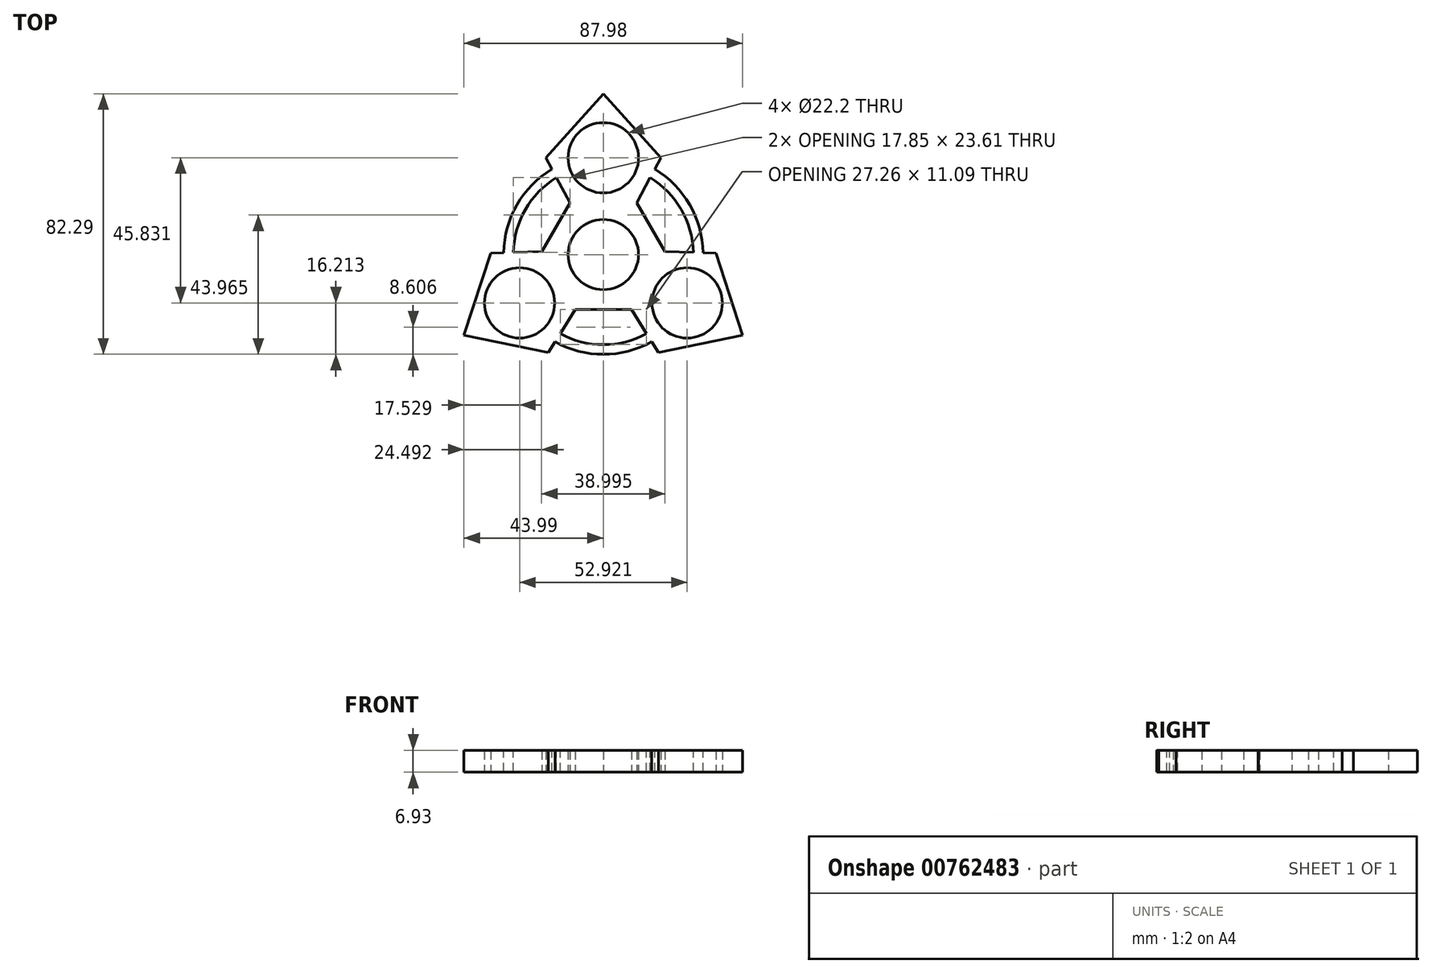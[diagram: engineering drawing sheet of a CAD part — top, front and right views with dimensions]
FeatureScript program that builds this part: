
annotation { "Feature Type Name" : "Feature", "Feature Type Description" : "" }
export const myFeature = defineFeature(function(context is Context, id is Id, definition is map)
    precondition{}
    {
        {
            var Q0;
            Q0=qCreatedBy(makeId("Top.planeOp"),FACE);
            var sketch = newSketch(context, id + "F0", { "sketchPlane" : qUnion([Q0])});
            skCircle(sketch, "E0", {"center": v(0, 0) * mm, "radius": 11.1 * mm});
            skLineSegment(sketch, "E1", {"start": v(0, 50.8) * mm, "end": v(18.14, 30.55) * mm});
            skLineSegment(sketch, "E2", {"start": v(18.14, 30.55) * mm, "end": v(10.57, 16.36) * mm});
            skLineSegment(sketch, "E3.MirrorCS", {"start": v(0, 50.8) * mm, "end": v(-18.14, 30.55) * mm});
            skLineSegment(sketch, "E4.MirrorCS", {"start": v(-18.14, 30.55) * mm, "end": v(-10.57, 16.36) * mm});
            skPoint(sketch, "E5.center.orphan", {"position": v(0, 30.55) * mm});
            skCircle(sketch, "E6", {"center": v(0, 30.55) * mm, "radius": 11.1 * mm});
            skLineSegment(sketch, "E7.1.0", {"start": v(-44, -25.4) * mm, "end": v(-35.53, 0.43) * mm});
            skLineSegment(sketch, "E7.1.1", {"start": v(-44, -25.4) * mm, "end": v(-17.4, -30.98) * mm});
            skCircle(sketch, "E7.1.2", {"center": v(-26.46, -15.28) * mm, "radius": 11.1 * mm});
            skLineSegment(sketch, "E7.1.3", {"start": v(-35.53, 0.43) * mm, "end": v(-19.46, 0.98) * mm});
            skLineSegment(sketch, "E7.1.4", {"start": v(-17.4, -30.98) * mm, "end": v(-8.88, -17.34) * mm});
            skLineSegment(sketch, "E7.2.0", {"start": v(44, -25.4) * mm, "end": v(17.4, -30.98) * mm});
            skLineSegment(sketch, "E7.2.1", {"start": v(44, -25.4) * mm, "end": v(35.53, 0.43) * mm});
            skCircle(sketch, "E7.2.2", {"center": v(26.46, -15.28) * mm, "radius": 11.1 * mm});
            skLineSegment(sketch, "E7.2.3", {"start": v(17.4, -30.98) * mm, "end": v(8.88, -17.34) * mm});
            skLineSegment(sketch, "E7.2.4", {"start": v(35.53, 0.43) * mm, "end": v(19.46, 0.98) * mm});
            skLineSegment(sketch, "E8", {"start": v(10.57, 16.36) * mm, "end": v(19.46, 0.98) * mm});
            skLineSegment(sketch, "E9", {"start": v(8.88, -17.34) * mm, "end": v(-8.88, -17.34) * mm});
            skLineSegment(sketch, "E10", {"start": v(-19.46, 0.98) * mm, "end": v(-10.57, 16.36) * mm});
            skSolve(sketch);
        }
        {
            var Q0;
            Q0=makeQuery(id+"F0.imprint","IMPRINT",FACE,{"disambiguationData":[TD([[makeQuery(id+"F0.imprint","IMPRINT",EDGE,{"derivedFrom":sQuery(id+"F0.wireOp",EDGE,"E0")}),-1.0]])]});
            extrude(context, id + "F1", {"entities" : qUnion([Q0]), "depth" : 6.93 * mm, "offsetDistance" : 25.4 * mm});
        }
        {
            var Q0;
            Q0=makeQuery(id+"F1.opExtrude","CAP_FACE",FACE,{"disambiguationData":[OSD([sQuery(id+"F0.wireOp",EDGE,"E0"),sQuery(id+"F0.wireOp",EDGE,"E1"),sQuery(id+"F0.wireOp",EDGE,"E2"),sQuery(id+"F0.wireOp",EDGE,"E3.MirrorCS"),sQuery(id+"F0.wireOp",EDGE,"E4.MirrorCS"),sQuery(id+"F0.wireOp",EDGE,"E6"),sQuery(id+"F0.wireOp",EDGE,"E7.1.0"),sQuery(id+"F0.wireOp",EDGE,"E7.1.1"),sQuery(id+"F0.wireOp",EDGE,"E7.1.2"),sQuery(id+"F0.wireOp",EDGE,"E7.1.3"),sQuery(id+"F0.wireOp",EDGE,"E7.1.4"),sQuery(id+"F0.wireOp",EDGE,"E7.2.0"),sQuery(id+"F0.wireOp",EDGE,"E7.2.1"),sQuery(id+"F0.wireOp",EDGE,"E7.2.2"),sQuery(id+"F0.wireOp",EDGE,"E7.2.3"),sQuery(id+"F0.wireOp",EDGE,"E7.2.4"),sQuery(id+"F0.wireOp",EDGE,"E8"),sQuery(id+"F0.wireOp",EDGE,"E9"),sQuery(id+"F0.wireOp",EDGE,"E10")])],"isStart":false});
            var sketch = newSketch(context, id + "F2", { "sketchPlane" : qUnion([Q0])});
            skCircle(sketch, "E11", {"center": v(0, 0) * mm, "radius": 28.43 * mm});
            skCircle(sketch, "E12", {"center": v(0, 0) * mm, "radius": 31.5 * mm});
            skSolve(sketch);
        }
        {
            var Q0;
            {var subQ0=sQuery(id+"F2.wireOp",EDGE,"E11");var subQ1=makeQuery(id+"F1.opExtrude","CAP_EDGE",EDGE,{"disambiguationData":[OSD([sQuery(id+"F0.wireOp",EDGE,"E7.1.4")])],"isStart":false});var subQ2=makeQuery(id+"F2.imprint","INTERSECT",VERTEX,{"derivedFrom":[subQ1,subQ0]});Q0=makeQuery(id+"F2.imprint","IMPRINT",FACE,{"disambiguationData":[TD([[makeQuery(id+"F2.imprint","IMPRINT",EDGE,{"disambiguationData":[TD([[subQ2,-1.0]])],"derivedFrom":subQ0}),-1.0]])]});}
            var Q1;
            {var subQ0=sQuery(id+"F2.wireOp",EDGE,"E11");var subQ1=makeQuery(id+"F1.opExtrude","CAP_EDGE",EDGE,{"disambiguationData":[OSD([sQuery(id+"F0.wireOp",EDGE,"E2")])],"isStart":false});var subQ2=makeQuery(id+"F2.imprint","INTERSECT",VERTEX,{"derivedFrom":[subQ1,subQ0]});Q1=makeQuery(id+"F2.imprint","IMPRINT",FACE,{"disambiguationData":[TD([[makeQuery(id+"F2.imprint","IMPRINT",EDGE,{"disambiguationData":[TD([[subQ2,1.0]])],"derivedFrom":subQ0}),-1.0]])]});}
            var Q2;
            {var subQ0=sQuery(id+"F2.wireOp",EDGE,"E11");var subQ1=makeQuery(id+"F1.opExtrude","CAP_EDGE",EDGE,{"disambiguationData":[OSD([sQuery(id+"F0.wireOp",EDGE,"E4.MirrorCS")])],"isStart":false});var subQ2=makeQuery(id+"F2.imprint","INTERSECT",VERTEX,{"derivedFrom":[subQ1,subQ0]});Q2=makeQuery(id+"F2.imprint","IMPRINT",FACE,{"disambiguationData":[TD([[makeQuery(id+"F2.imprint","IMPRINT",EDGE,{"disambiguationData":[TD([[subQ2,-1.0]])],"derivedFrom":subQ0}),-1.0]])]});}
            extrude(context, id + "F3", {"entities" : qUnion([Q0, Q1, Q2]), "operationType" : NewBodyOperationType.ADD, "oppositeDirection" : true, "depth" : 6.93 * mm, "offsetDistance" : 25.4 * mm});
        }
    });
